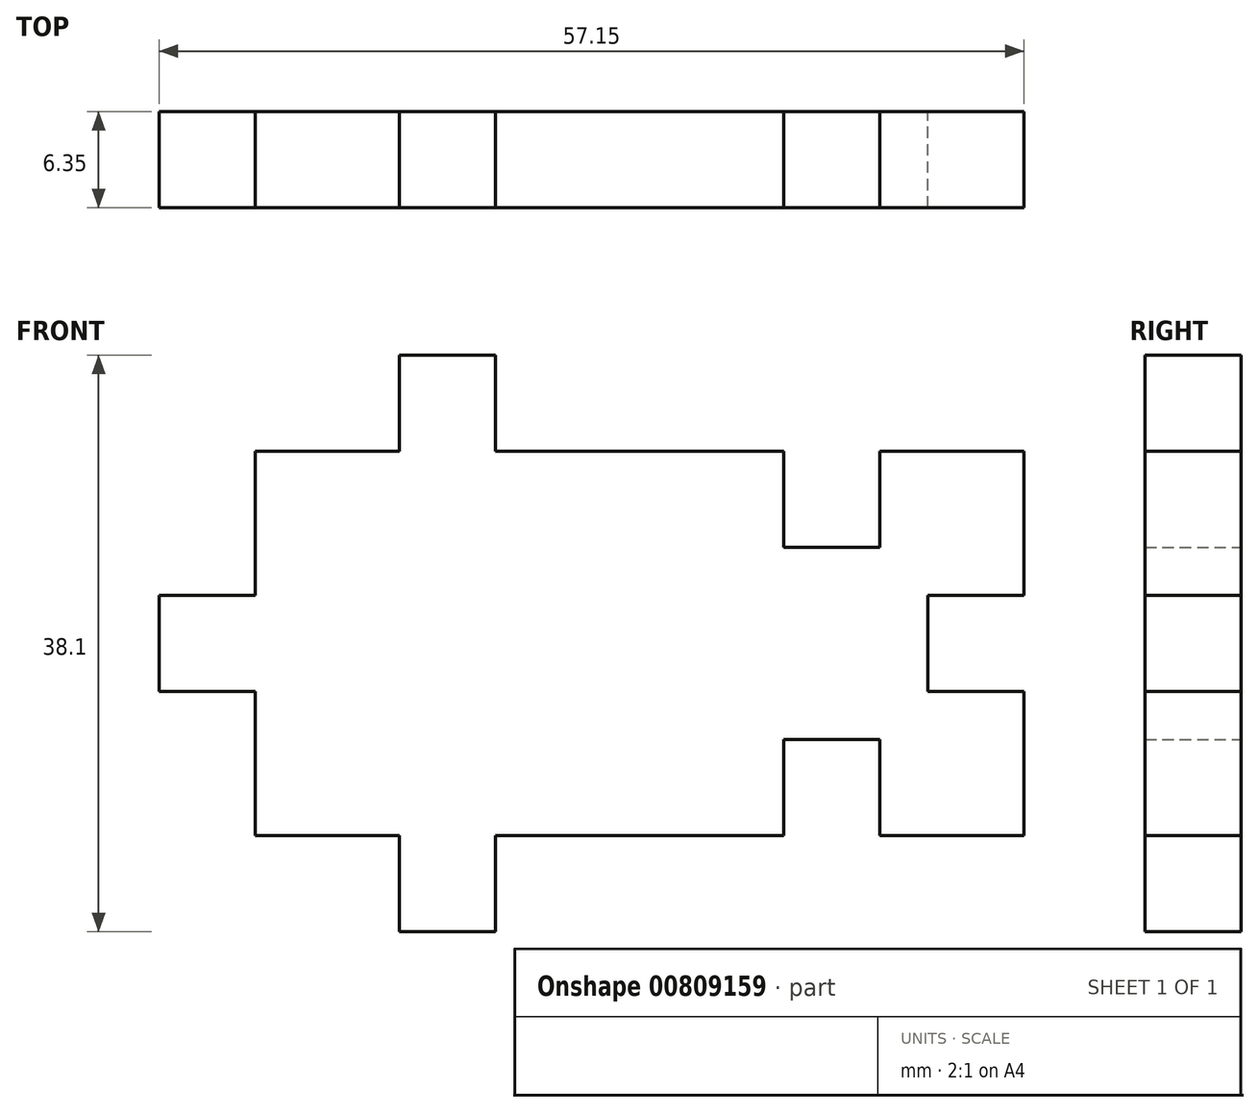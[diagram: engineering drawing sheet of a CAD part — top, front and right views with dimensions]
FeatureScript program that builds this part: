
annotation { "Feature Type Name" : "Feature", "Feature Type Description" : "" }
export const myFeature = defineFeature(function(context is Context, id is Id, definition is map)
    precondition{}
    {
        {
            var Q0;
            Q0=qCreatedBy(makeId("Front.planeOp"),FACE);
            var sketch = newSketch(context, id + "F0", { "sketchPlane" : qUnion([Q0])});
            skLineSegment(sketch, "E0", {"start": v(0, 0) * mm, "end": v(0, 12.7) * mm});
            skLineSegment(sketch, "E1", {"start": v(0, 12.7) * mm, "end": v(-9.53, 12.7) * mm});
            skLineSegment(sketch, "E2", {"start": v(19.05, 3.18) * mm, "end": v(25.4, 3.18) * mm});
            skLineSegment(sketch, "E3", {"start": v(0, 12.7) * mm, "end": v(9.53, 12.7) * mm});
            skLineSegment(sketch, "E4", {"start": v(25.4, 12.7) * mm, "end": v(25.4, 3.18) * mm});
            skLineSegment(sketch, "E5", {"start": v(25.4, 0) * mm, "end": v(25.4, 0) * mm});
            skLineSegment(sketch, "E6.MirrorCS", {"start": v(25.4, -12.7) * mm, "end": v(25.4, -3.18) * mm});
            skLineSegment(sketch, "E7.MirrorCS", {"start": v(0, -12.7) * mm, "end": v(9.53, -12.7) * mm});
            skLineSegment(sketch, "E8.MirrorCS", {"start": v(0, -12.7) * mm, "end": v(-9.53, -12.7) * mm});
            skLineSegment(sketch, "E9.MirrorCS", {"start": v(19.05, -3.18) * mm, "end": v(25.4, -3.18) * mm});
            skPoint(sketch, "E10.orphan", {"position": v(19.05, 0) * mm});
            skLineSegment(sketch, "E11.trimOffspring", {"start": v(9.53, 12.7) * mm, "end": v(-9.53, 12.7) * mm});
            skPoint(sketch, "E12.start.orphan", {"position": v(9.53, 12.7) * mm});
            skLineSegment(sketch, "E13", {"start": v(-9.53, -12.7) * mm, "end": v(-9.53, -19.05) * mm});
            skLineSegment(sketch, "E14", {"start": v(-15.88, -12.7) * mm, "end": v(-15.88, -19.05) * mm});
            skLineSegment(sketch, "E15", {"start": v(-9.53, -19.05) * mm, "end": v(-15.88, -19.05) * mm});
            skLineSegment(sketch, "E16.trimOffspring", {"start": v(9.53, -12.7) * mm, "end": v(0, -12.7) * mm});
            skPoint(sketch, "E17.orphan", {"position": v(9.53, -12.7) * mm});
            skLineSegment(sketch, "E18.MirrorCS", {"start": v(-25.4, 12.7) * mm, "end": v(-25.4, 3.17) * mm});
            skLineSegment(sketch, "E19.MirrorCS", {"start": v(-25.4, -12.7) * mm, "end": v(-25.4, -3.18) * mm});
            skLineSegment(sketch, "E20.trimOffspring", {"start": v(-15.88, -12.7) * mm, "end": v(-25.4, -12.7) * mm});
            skPoint(sketch, "E21.orphan", {"position": v(-25.4, 0) * mm});
            skPoint(sketch, "E22.MirrorCS.start.orphan", {"position": v(-25.4, 12.7) * mm});
            skLineSegment(sketch, "E23.trimOffspring", {"start": v(-15.88, 12.7) * mm, "end": v(-25.4, 12.7) * mm});
            skLineSegment(sketch, "E24", {"start": v(9.53, -12.7) * mm, "end": v(9.53, -6.35) * mm});
            skLineSegment(sketch, "E25", {"start": v(9.53, -6.35) * mm, "end": v(15.88, -6.35) * mm});
            skLineSegment(sketch, "E26", {"start": v(15.88, -12.7) * mm, "end": v(15.88, -6.35) * mm});
            skLineSegment(sketch, "E27.trimOffspring", {"start": v(19.05, -12.7) * mm, "end": v(15.88, -12.7) * mm});
            skLineSegment(sketch, "E28.trimOffspring", {"start": v(15.88, -12.7) * mm, "end": v(25.4, -12.7) * mm});
            skPoint(sketch, "E29.orphan", {"position": v(12.7, -12.7) * mm});
            skLineSegment(sketch, "E30", {"start": v(19.05, 3.18) * mm, "end": v(19.05, -3.18) * mm});
            skPoint(sketch, "E31.MirrorCS.start.orphan", {"position": v(19.05, -12.7) * mm});
            skPoint(sketch, "E32.orphan", {"position": v(25.4, 0) * mm});
            skLineSegment(sketch, "E33", {"start": v(-15.88, 12.7) * mm, "end": v(-15.88, 19.05) * mm});
            skLineSegment(sketch, "E34", {"start": v(-15.88, 19.05) * mm, "end": v(-9.53, 19.05) * mm});
            skLineSegment(sketch, "E35", {"start": v(-9.53, 12.7) * mm, "end": v(-9.53, 19.05) * mm});
            skPoint(sketch, "E36.end.orphan", {"position": v(-9.53, 6.35) * mm});
            skPoint(sketch, "E37.end.orphan", {"position": v(-15.88, 6.35) * mm});
            skLineSegment(sketch, "E38", {"start": v(19.05, 12.7) * mm, "end": v(15.88, 12.7) * mm});
            skLineSegment(sketch, "E39", {"start": v(15.88, 12.7) * mm, "end": v(15.88, 6.35) * mm});
            skLineSegment(sketch, "E40", {"start": v(15.88, 6.35) * mm, "end": v(9.53, 6.35) * mm});
            skLineSegment(sketch, "E41", {"start": v(9.53, 6.35) * mm, "end": v(9.53, 12.7) * mm});
            skLineSegment(sketch, "E42.trimOffspring", {"start": v(15.88, 12.7) * mm, "end": v(25.4, 12.7) * mm});
            skPoint(sketch, "E43.orphan", {"position": v(12.7, 12.7) * mm});
            skPoint(sketch, "E44.end.orphan", {"position": v(-19.05, -3.18) * mm});
            skLineSegment(sketch, "E45", {"start": v(-25.4, 3.17) * mm, "end": v(-31.75, 3.17) * mm});
            skLineSegment(sketch, "E46", {"start": v(-31.75, 3.17) * mm, "end": v(-31.75, -3.18) * mm});
            skLineSegment(sketch, "E47", {"start": v(-25.4, -3.18) * mm, "end": v(-31.75, -3.18) * mm});
            skSolve(sketch);
        }
        {
            var Q0;
            Q0=makeQuery(id+"F0.imprint","IMPRINT",FACE,{"disambiguationData":[TD([[makeQuery(id+"F0.imprint","IMPRINT",EDGE,{"derivedFrom":sQuery(id+"F0.wireOp",EDGE,"E2")}),1.0]])]});
            extrude(context, id + "F1", {"entities" : qUnion([Q0]), "depth" : 6.35 * mm, "offsetDistance" : 25.4 * mm});
        }
    });
